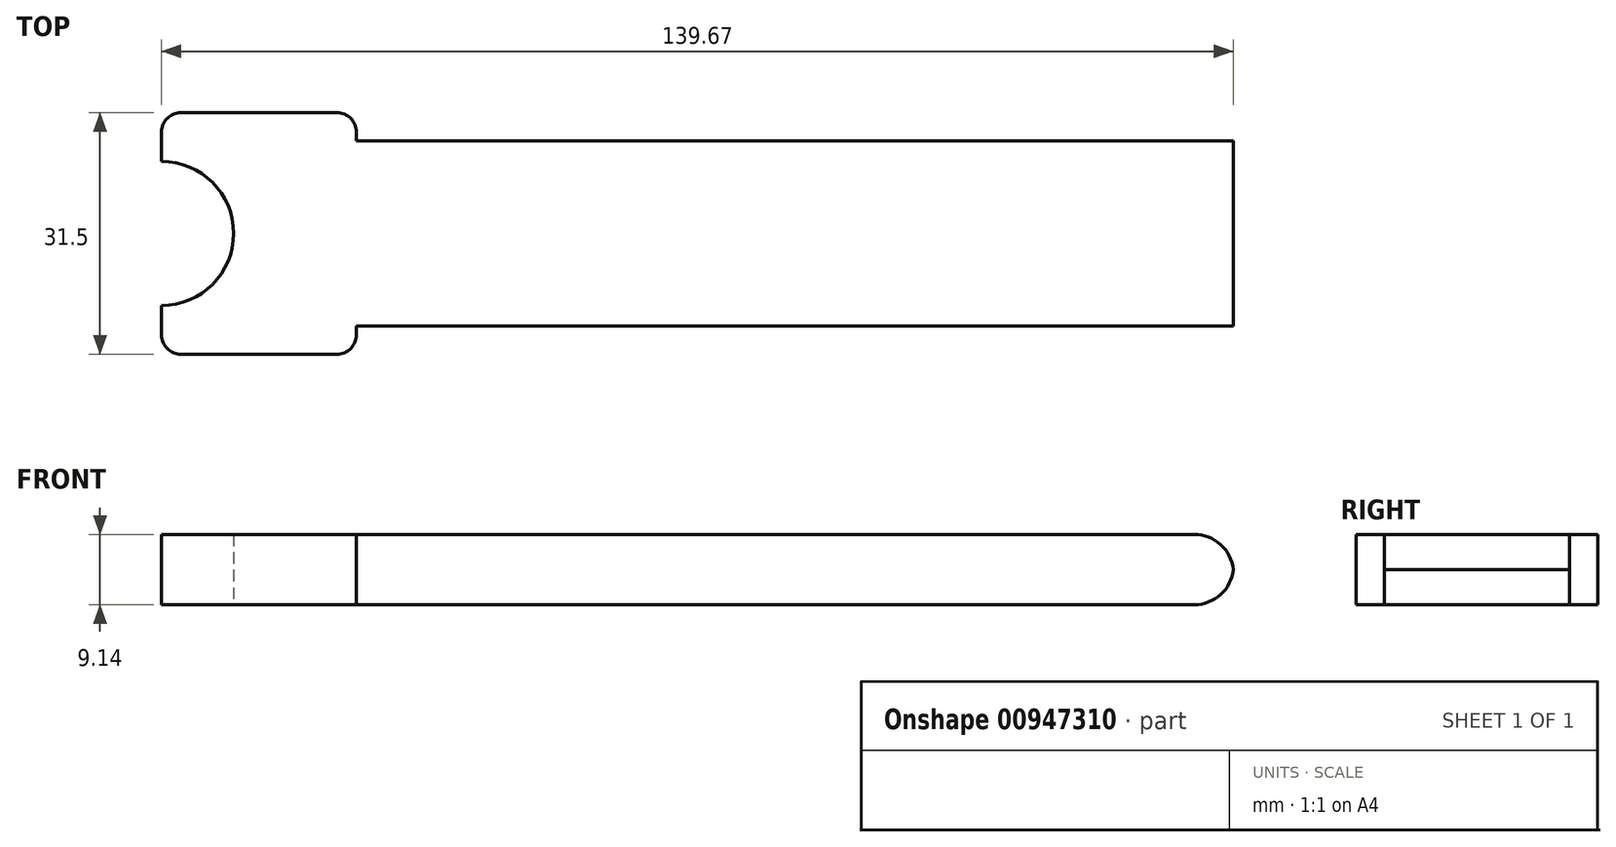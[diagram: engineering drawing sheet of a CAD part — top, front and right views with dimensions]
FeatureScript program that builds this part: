
annotation { "Feature Type Name" : "Feature", "Feature Type Description" : "" }
export const myFeature = defineFeature(function(context is Context, id is Id, definition is map)
    precondition{}
    {
        {
            var Q0;
            Q0=qCreatedBy(makeId("Top.planeOp"),FACE);
            var sketch = newSketch(context, id + "F0", { "sketchPlane" : qUnion([Q0])});
            skArc(sketch, "E0", {"start": v(0, -9.4) * mm, "mid": v(9.4, 0) * mm, "end": v(0, 9.4) * mm});
            skLineSegment(sketch, "E1", {"start": v(0, 9.4) * mm, "end": v(0, 15.75) * mm});
            skLineSegment(sketch, "E2", {"start": v(0, 15.75) * mm, "end": v(25.4, 15.75) * mm});
            skLineSegment(sketch, "E3", {"start": v(0, -9.4) * mm, "end": v(0, -15.75) * mm});
            skLineSegment(sketch, "E4", {"start": v(0, -15.75) * mm, "end": v(25.4, -15.75) * mm});
            skLineSegment(sketch, "E5", {"start": v(25.4, -15.75) * mm, "end": v(25.4, 15.75) * mm});
            skSolve(sketch);
        }
        {
            var Q0;
            Q0 = qSketchRegion(id + "F0", true);
            extrude(context, id + "F1", {"entities" : qUnion([Q0]), "depth" : 9.14 * mm, "offsetDistance" : 25.4 * mm});
        }
        {
            var Q0;
            Q0=makeQuery(id+"F1.opExtrude","SWEPT_EDGE",EDGE,{"disambiguationData":[OSD([sQuery(id+"F0.wireOp",EDGE,"E4"),sQuery(id+"F0.wireOp",EDGE,"E5")])]});
            var Q1;
            Q1=makeQuery(id+"F1.opExtrude","SWEPT_EDGE",EDGE,{"disambiguationData":[OSD([sQuery(id+"F0.wireOp",EDGE,"E3"),sQuery(id+"F0.wireOp",EDGE,"E4")])]});
            var Q2;
            Q2=makeQuery(id+"F1.opExtrude","SWEPT_EDGE",EDGE,{"disambiguationData":[OSD([sQuery(id+"F0.wireOp",EDGE,"E1"),sQuery(id+"F0.wireOp",EDGE,"E2")])]});
            var Q3;
            Q3=makeQuery(id+"F1.opExtrude","SWEPT_EDGE",EDGE,{"disambiguationData":[OSD([sQuery(id+"F0.wireOp",EDGE,"E2"),sQuery(id+"F0.wireOp",EDGE,"E5")])]});
            fillet(context, id + "F2", {"entities" : qUnion([Q0, Q1, Q2, Q3]), "radius" : 2.54 * mm, "tangentPropagation" : true, "allowEdgeOverflow" : false});
        }
        {
            var Q0;
            Q0=makeQuery(id+"F1.opExtrude","SWEPT_FACE",FACE,{"disambiguationData":[OSD([sQuery(id+"F0.wireOp",EDGE,"E5")])]});
            var sketch = newSketch(context, id + "F3", { "sketchPlane" : qUnion([Q0])});
            skLineSegment(sketch, "E6.bottom", {"start": v(-12.07, 9.14) * mm, "end": v(12.06, 9.14) * mm});
            skLineSegment(sketch, "E6.top", {"start": v(-12.07, 0) * mm, "end": v(12.06, 0) * mm});
            skLineSegment(sketch, "E6.left", {"start": v(-12.07, 9.14) * mm, "end": v(-12.07, 0) * mm});
            skLineSegment(sketch, "E6.right", {"start": v(12.06, 9.14) * mm, "end": v(12.06, 0) * mm});
            skSolve(sketch);
        }
        {
            var Q0;
            Q0=makeQuery(id+"F3.imprint","IMPRINT",FACE,{"disambiguationData":[TD([[makeQuery(id+"F3.imprint","IMPRINT",EDGE,{"derivedFrom":sQuery(id+"F3.wireOp",EDGE,"E6.bottom")}),-1.0]])]});
            extrude(context, id + "F4", {"entities" : qUnion([Q0]), "operationType" : NewBodyOperationType.ADD, "depth" : 114.3 * mm, "offsetDistance" : 25.4 * mm});
        }
        {
            var Q0;
            Q0=makeQuery(id+"F4.opExtrude","CAP_EDGE",EDGE,{"disambiguationData":[OSD([sQuery(id+"F3.wireOp",EDGE,"E6.bottom")])],"isStart":false});
            var Q1;
            Q1=makeQuery(id+"F4.opExtrude","CAP_EDGE",EDGE,{"disambiguationData":[OSD([sQuery(id+"F3.wireOp",EDGE,"E6.top")])],"isStart":false});
            fillet(context, id + "F5", {"entities" : qUnion([Q0, Q1]), "radius" : 5.08 * mm, "tangentPropagation" : true, "allowEdgeOverflow" : false});
        }
    });
